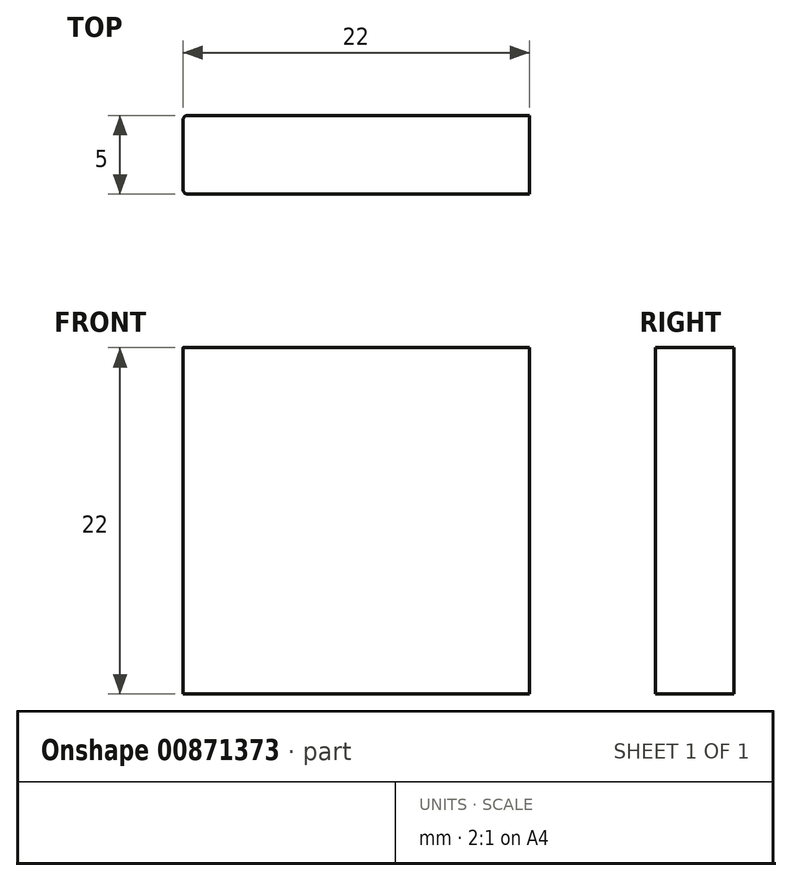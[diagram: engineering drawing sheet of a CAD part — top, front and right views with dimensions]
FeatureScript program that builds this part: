
annotation { "Feature Type Name" : "Feature", "Feature Type Description" : "" }
export const myFeature = defineFeature(function(context is Context, id is Id, definition is map)
    precondition{}
    {
        {
            var Q0;
            Q0=qCreatedBy(makeId("Top.planeOp"),FACE);
            var sketch = newSketch(context, id + "F0", { "sketchPlane" : qUnion([Q0])});
            skLineSegment(sketch, "E0.bottom", {"start": v(-0.67, -4.82) * mm, "end": v(21.03, -4.82) * mm});
            skLineSegment(sketch, "E0.top", {"start": v(-0.67, -9.82) * mm, "end": v(21.03, -9.82) * mm});
            skLineSegment(sketch, "E0.left", {"start": v(-0.97, -5.12) * mm, "end": v(-0.97, -9.52) * mm});
            skLineSegment(sketch, "E0.right", {"start": v(21.03, -4.82) * mm, "end": v(21.03, -9.82) * mm});
            skPoint(sketch, "E1.visualSharp", {"position": v(-0.97, -9.82) * mm});
            skArc(sketch, "E1.filletArc", {"start": v(-0.97, -9.52) * mm, "mid": v(-0.88, -9.73) * mm, "end": v(-0.67, -9.82) * mm});
            skPoint(sketch, "E2.visualSharp", {"position": v(-0.97, -4.82) * mm});
            skArc(sketch, "E2.filletArc", {"start": v(-0.67, -4.82) * mm, "mid": v(-0.88, -4.9) * mm, "end": v(-0.97, -5.12) * mm});
            skSolve(sketch);
        }
        {
            var Q0;
            Q0 = qSketchRegion(id + "F0", true);
            extrude(context, id + "F1", {"entities" : qUnion([Q0]), "depth" : 22 * mm, "offsetDistance" : 25 * mm});
        }
    });
